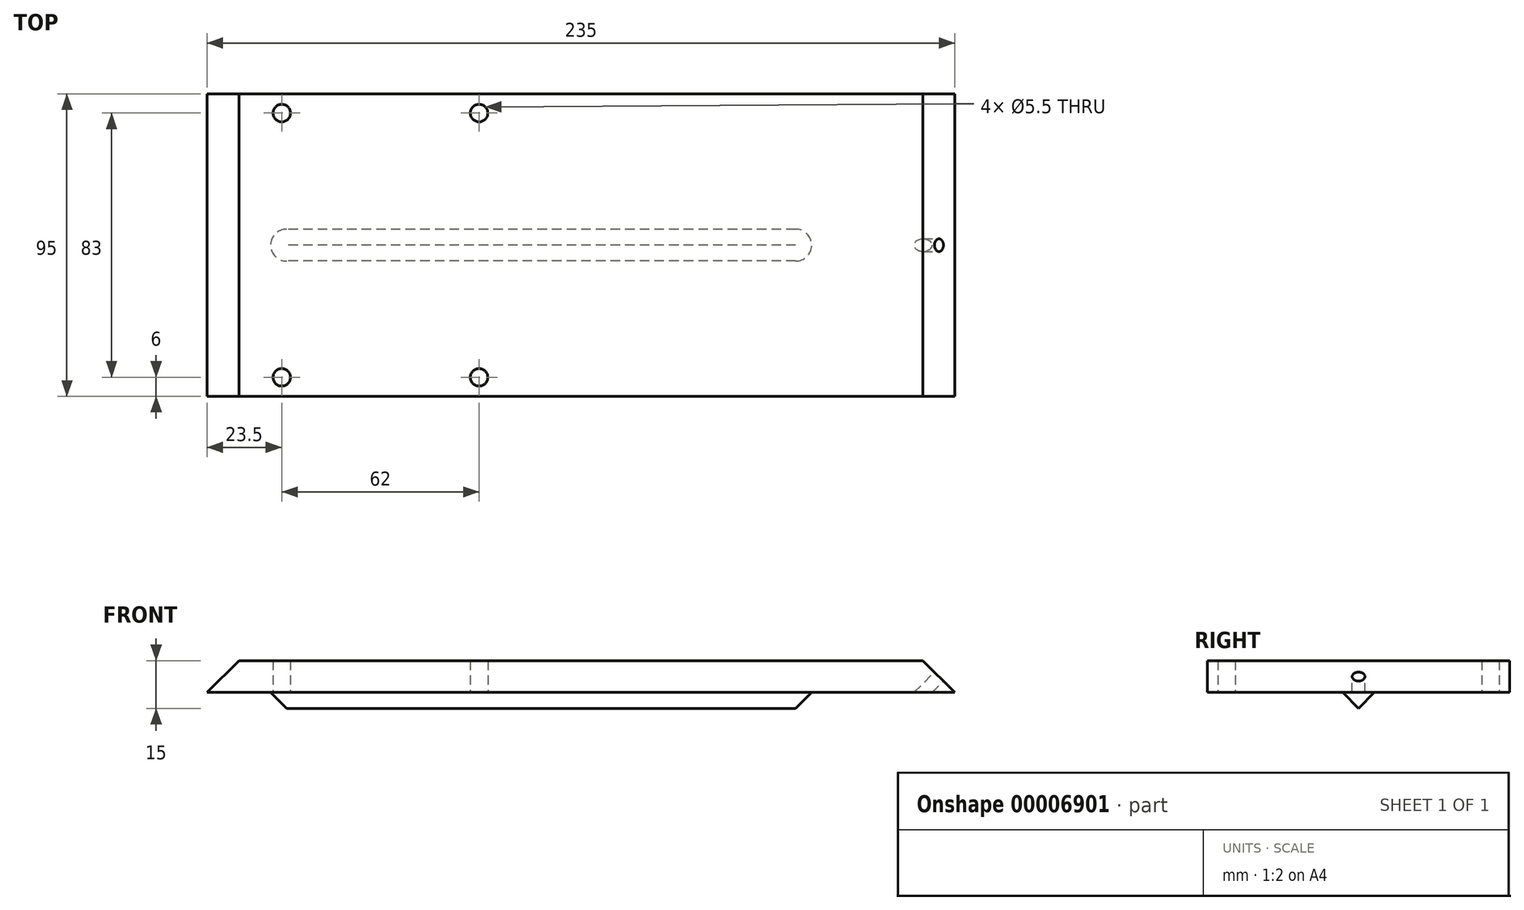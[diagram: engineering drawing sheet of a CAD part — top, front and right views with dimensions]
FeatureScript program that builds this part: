
annotation { "Feature Type Name" : "Feature", "Feature Type Description" : "" }
export const myFeature = defineFeature(function(context is Context, id is Id, definition is map)
    precondition{}
    {
        {
            var Q0;
            Q0=qCreatedBy(makeId("Top.planeOp"),FACE);
            var sketch = newSketch(context, id + "F0", { "sketchPlane" : qUnion([Q0])});
            skLineSegment(sketch, "E0.rect.bottom", {"start": v(125, -47.5) * mm, "end": v(-125, -47.5) * mm});
            skLineSegment(sketch, "E0.rect.top", {"start": v(125, 47.5) * mm, "end": v(-125, 47.5) * mm});
            skLineSegment(sketch, "E0.rect.left", {"start": v(125, -47.5) * mm, "end": v(125, 47.5) * mm});
            skLineSegment(sketch, "E0.rect.right", {"start": v(-125, -47.5) * mm, "end": v(-125, 47.5) * mm});
            skPoint(sketch, "E0.rect.middle", {"position": v(0, 0) * mm});
            skLineSegment(sketch, "E1", {"start": v(-125, 0) * mm, "end": v(125, 0) * mm, "construction": true});
            skLineSegment(sketch, "E2", {"start": v(-101.5, 47.5) * mm, "end": v(-101.5, -47.5) * mm, "construction": true});
            skLineSegment(sketch, "E3", {"start": v(-39.5, 47.5) * mm, "end": v(-39.5, -47.5) * mm, "construction": true});
            skLineSegment(sketch, "E4", {"start": v(-25.5, 47.5) * mm, "end": v(-25.5, -47.5) * mm, "construction": true});
            skCircle(sketch, "E5", {"center": v(-101.5, 41.5) * mm, "radius": 2.75 * mm});
            skCircle(sketch, "E6", {"center": v(-39.5, 41.5) * mm, "radius": 2.75 * mm});
            skCircle(sketch, "E7", {"center": v(-101.5, -41.5) * mm, "radius": 2.75 * mm});
            skCircle(sketch, "E8", {"center": v(-39.5, -41.5) * mm, "radius": 2.75 * mm});
            skSolve(sketch);
        }
        {
            var Q0;
            Q0=qSketchRegion(id+"F0",true);
            var Q1;
            Q1=makeQuery(id+"F0.imprint","IMPRINT",FACE,{"disambiguationData":[TD([[makeQuery(id+"F0.imprint","IMPRINT",EDGE,{"derivedFrom":sQuery(id+"F0.wireOp",EDGE,"E0.rect.bottom")}),-1.0]])]});
            extrude(context, id + "F1", {"entities" : qUnion([Q0, Q1]), "depth" : (15) * mm});
        }
        {
            var Q0;
            Q0=makeQuery(id+"F1.opExtrude","SWEPT_FACE",FACE,{"disambiguationData":[OSD([sQuery(id+"F0.wireOp",EDGE,"E0.rect.right")])]});
            var sketch = newSketch(context, id + "F2", { "sketchPlane" : qUnion([Q0])});
            skLineSegment(sketch, "E9", {"start": v(0, 0) * mm, "end": v(-5, 5) * mm});
            skLineSegment(sketch, "E10", {"start": v(0, 0) * mm, "end": v(5, 5) * mm});
            skLineSegment(sketch, "E11", {"start": v(-5, 5) * mm, "end": v(-47.5, 5) * mm});
            skLineSegment(sketch, "E12", {"start": v(5, 5) * mm, "end": v(47.5, 5) * mm});
            skSolve(sketch);
        }
        {
            var Q0;
            Q0=qSketchRegion(id+"F2",true);
            var Q1;
            {var subQ2=sQuery(id+"F2.wireOp",EDGE,"E9");Q1=makeQuery(id+"F2.imprint","IMPRINT",FACE,{"disambiguationData":[TD([[makeQuery(id+"F2.imprint","IMPRINT",EDGE,{"derivedFrom":subQ2}),1.0]])]});}
            var Q2;
            {var subQ2=sQuery(id+"F2.wireOp",EDGE,"E10");Q2=makeQuery(id+"F2.imprint","IMPRINT",FACE,{"disambiguationData":[TD([[makeQuery(id+"F2.imprint","IMPRINT",EDGE,{"derivedFrom":subQ2}),-1.0]])]});}
            extrude(context, id + "F3", {"entities" : qUnion([Q0, Q1, Q2]), "operationType" : NewBodyOperationType.REMOVE, "endBound" : BoundingType.THROUGH_ALL, "oppositeDirection" : true, "depth" : 25 * mm});
        }
        {
            var Q0;
            Q0=makeQuery(id+"F1.opExtrude","SWEPT_FACE",FACE,{"disambiguationData":[OSD([sQuery(id+"F0.wireOp",EDGE,"E0.rect.right")])]});
            var sketch = newSketch(context, id + "F4", { "sketchPlane" : qUnion([Q0])});
            skLineSegment(sketch, "E13", {"start": v(-5, 5) * mm, "end": v(5, 5) * mm});
            skSolve(sketch);
        }
        {
            var Q0;
            Q0=qSketchRegion(id+"F4",true);
            var Q1;
            Q1=makeQuery(id+"F4.imprint","IMPRINT",FACE,{"disambiguationData":[TD([[makeQuery(id+"F4.imprint","IMPRINT",EDGE,{"derivedFrom":sQuery(id+"F4.wireOp",EDGE,"E13")}),-1.0]])]});
            extrude(context, id + "F5", {"entities" : qUnion([Q0, Q1]), "operationType" : NewBodyOperationType.REMOVE, "oppositeDirection" : true, "depth" : 25 * mm});
        }
        {
            var Q0;
            Q0=makeQuery(id+"F5.boolean.opBoolean","COPY",FACE,{"derivedFrom":makeQuery(id+"F5.opExtrude","CAP_FACE",FACE,{"disambiguationData":[OSD([sQuery(id+"F2.wireOp",EDGE,"E9"),sQuery(id+"F2.wireOp",EDGE,"E10"),sQuery(id+"F4.wireOp",EDGE,"E13")])],"isStart":false})});
            var sketch = newSketch(context, id + "F6", { "sketchPlane" : qUnion([Q0])});
            skLineSegment(sketch, "E14", {"start": v(0, 0) * mm, "end": v(0, 5) * mm});
            skSolve(sketch);
        }
        {
            var Q0;
            {var subQ1=sQuery(id+"F6.wireOp",EDGE,"E14");Q0=makeQuery(id+"F6.imprint","IMPRINT",FACE,{"disambiguationData":[TD([[makeQuery(id+"F6.imprint","IMPRINT",EDGE,{"derivedFrom":subQ1}),1.0]])]});}
            var Q1;
            Q1=sQuery(id+"F6.wireOp",EDGE,"E14");
            revolve(context, id + "F7", {"operationType" : NewBodyOperationType.ADD, "entities" : qUnion([Q0]), "axis" : qUnion([Q1]), "revolveType" : RevolveType.FULL});
        }
        {
            var Q0;
            Q0=makeQuery(id+"F1.opExtrude","SWEPT_FACE",FACE,{"disambiguationData":[OSD([sQuery(id+"F0.wireOp",EDGE,"E0.rect.top")])]});
            var sketch = newSketch(context, id + "F8", { "sketchPlane" : qUnion([Q0])});
            skLineSegment(sketch, "E15", {"start": v(125, 5) * mm, "end": v(115, 15) * mm});
            skSolve(sketch);
        }
        {
            var Q0;
            Q0=qSketchRegion(id+"F8",true);
            var Q1;
            {var subQ2=sQuery(id+"F8.wireOp",EDGE,"E15");Q1=makeQuery(id+"F8.imprint","IMPRINT",FACE,{"disambiguationData":[TD([[makeQuery(id+"F8.imprint","IMPRINT",EDGE,{"derivedFrom":subQ2}),-1.0]])]});}
            extrude(context, id + "F9", {"entities" : qUnion([Q0, Q1]), "operationType" : NewBodyOperationType.REMOVE, "endBound" : BoundingType.THROUGH_ALL, "oppositeDirection" : true, "depth" : 25 * mm});
        }
        {
            var Q0;
            Q0=makeQuery(id+"F1.opExtrude","SWEPT_FACE",FACE,{"disambiguationData":[OSD([sQuery(id+"F0.wireOp",EDGE,"E0.rect.left")])]});
            extrude(context, id + "F10", {"entities" : qUnion([Q0]), "operationType" : NewBodyOperationType.REMOVE, "oppositeDirection" : true, "depth" : (15) * mm});
        }
        {
            var Q0;
            Q0=makeQuery(id+"F10.boolean.opBoolean","COPY",FACE,{"derivedFrom":makeQuery(id+"F10.opExtrude","CAP_FACE",FACE,{"disambiguationData":[OSD([sQuery(id+"F0.wireOp",EDGE,"E0.rect.left")])],"isStart":false})});
            var sketch = newSketch(context, id + "F11", { "sketchPlane" : qUnion([Q0])});
            skLineSegment(sketch, "E16", {"start": v(-5, 5) * mm, "end": v(5, 5) * mm});
            skSolve(sketch);
        }
        {
            var Q0;
            Q0=makeQuery(id+"F11.imprint","IMPRINT",FACE,{"disambiguationData":[TD([[makeQuery(id+"F11.imprint","IMPRINT",EDGE,{"derivedFrom":sQuery(id+"F11.wireOp",EDGE,"E16")}),-1.0]])]});
            extrude(context, id + "F12", {"entities" : qUnion([Q0]), "operationType" : NewBodyOperationType.REMOVE, "oppositeDirection" : true, "depth" : (50) * mm});
        }
        {
            var Q0;
            Q0=makeQuery(id+"F12.boolean.opBoolean","COPY",FACE,{"derivedFrom":makeQuery(id+"F12.opExtrude","CAP_FACE",FACE,{"disambiguationData":[OSD([sQuery(id+"F0.wireOp",EDGE,"E0.rect.left"),sQuery(id+"F2.wireOp",EDGE,"E9"),sQuery(id+"F2.wireOp",EDGE,"E10"),sQuery(id+"F11.wireOp",EDGE,"E16")])],"isStart":false})});
            var sketch = newSketch(context, id + "F13", { "sketchPlane" : qUnion([Q0])});
            skLineSegment(sketch, "E17", {"start": v(0, 0) * mm, "end": v(0, 5) * mm});
            skSolve(sketch);
        }
        {
            var Q0;
            {var subQ1=sQuery(id+"F13.wireOp",EDGE,"E17");Q0=makeQuery(id+"F13.imprint","IMPRINT",FACE,{"disambiguationData":[TD([[makeQuery(id+"F13.imprint","IMPRINT",EDGE,{"derivedFrom":subQ1}),-1.0]])]});}
            var Q1;
            Q1=sQuery(id+"F13.wireOp",EDGE,"E17");
            revolve(context, id + "F14", {"operationType" : NewBodyOperationType.ADD, "entities" : qUnion([Q0]), "axis" : qUnion([Q1]), "revolveType" : RevolveType.FULL});
        }
        {
            var Q0;
            Q0=makeQuery(id+"F1.opExtrude","SWEPT_FACE",FACE,{"disambiguationData":[OSD([sQuery(id+"F0.wireOp",EDGE,"E0.rect.top")])]});
            var sketch = newSketch(context, id + "F15", { "sketchPlane" : qUnion([Q0])});
            skLineSegment(sketch, "E18", {"start": v(-110, 5) * mm, "end": v(-100, 15) * mm});
            skSolve(sketch);
        }
        {
            var Q0;
            Q0=qSketchRegion(id+"F15",true);
            var Q1;
            {var subQ2=sQuery(id+"F15.wireOp",EDGE,"E18");Q1=makeQuery(id+"F15.imprint","IMPRINT",FACE,{"disambiguationData":[TD([[makeQuery(id+"F15.imprint","IMPRINT",EDGE,{"derivedFrom":subQ2}),1.0]])]});}
            extrude(context, id + "F16", {"entities" : qUnion([Q0, Q1]), "operationType" : NewBodyOperationType.REMOVE, "endBound" : BoundingType.THROUGH_ALL, "oppositeDirection" : true, "depth" : 25 * mm});
        }
        {
            var Q0;
            Q0=makeQuery(id+"F16.boolean.opBoolean","COPY",FACE,{"derivedFrom":makeQuery(id+"F16.opExtrude","SWEPT_FACE",FACE,{"disambiguationData":[OSD([sQuery(id+"F15.wireOp",EDGE,"E18")])]})});
            var sketch = newSketch(context, id + "F17", { "sketchPlane" : qUnion([Q0])});
            skLineSegment(sketch, "E19", {"start": v(0, -60.1) * mm, "end": v(0, -74.25) * mm, "construction": true});
            skCircle(sketch, "E20", {"center": v(0, -67.18) * mm, "radius": 2 * mm});
            skSolve(sketch);
        }
        {
            var Q0;
            Q0=qSketchRegion(id+"F17",true);
            extrude(context, id + "F18", {"entities" : qUnion([Q0]), "operationType" : NewBodyOperationType.REMOVE, "endBound" : BoundingType.THROUGH_ALL, "oppositeDirection" : true, "depth" : 25 * mm});
        }
    });
